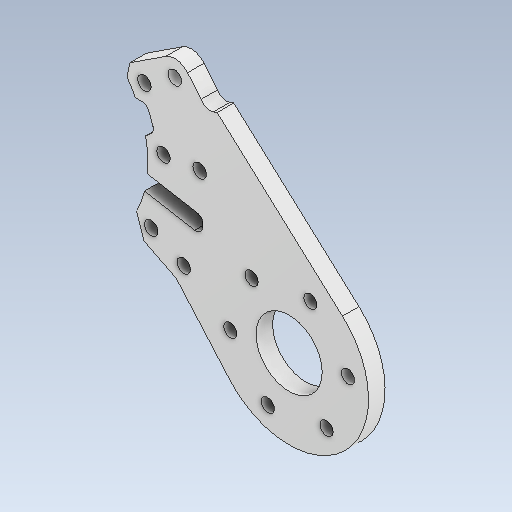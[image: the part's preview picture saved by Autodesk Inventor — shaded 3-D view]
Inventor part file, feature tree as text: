
AUTODESK INVENTOR PART (.ipt)
format: ipt  version: 2020 (Build 240168000, 168)  size: 461,312 bytes
history: native  units: mm
features: reference x17, extrude x7, sketch x7, thicken_offset x4, other x4, projected_geometry x3, chamfer x2, fillet x1, shell x1
ambient origin geometry x8: Origin, YZ Plane, XZ Plane, XY Plane, X Axis, Y Axis, Z Axis, Center Point
bodies: Solid1 (feature_tree)
feature tree (46):
  extrude  "Extrusion1"  Depth=10.0mm
  extrude  "Extrusion2"  Depth=10.0mm
  extrude  "Extrusion3"  Depth=5.0mm TaperAngle=0.0deg
  extrude  "Extrusion4"  Depth=5.0mm
  chamfer  "Chamfer1"  Distance=5.0mm
  chamfer  "Chamfer2"  Distance=5.0mm
  extrude  "Extrusion5"  Depth=5.0mm TaperAngle=45.0deg
  extrude  "Extrusion6"  Depth=5.0mm
  extrude  "Extrusion7"  Depth=5.0mm
  thicken_offset  "Thicken1"
  thicken_offset  "Thicken2"
  thicken_offset  "Thicken3"
  thicken_offset  "Thicken4"
  fillet  "Fillet1"  Radius=5.0mm
  sketch  "Sketch1"  dims[d0=48.0mm d1=10.0mm]
  reference  "Reference1"
  reference  "Reference2"
  reference  "Reference3"
  reference  "Reference4"
  reference  "Reference5"
  reference  "Reference6"
  reference  "Reference7"
  reference  "Reference8"
  reference  "Reference9"
  sketch  "Sketch2"  dims[d2=10.0mm d3=10.0mm]
  projected_geometry  "Projected Loop1"
  sketch  "Sketch3"  dims[d4=64.0mm d5=5.0mm d6=0.0mm]
  reference  "Reference10"
  sketch  "Sketch4"  dims[d7=5.0mm d8=0.0mm d9=5.0mm]
  projected_geometry  "Projected Loop2"
  sketch  "Sketch5"  dims[d10=16.0mm d11=5.0mm d12=0.0mm]
  reference  "Reference11"
  sketch  "Sketch6"  dims[d13=20.0mm d14=5.0mm d15=0.0mm]
  projected_geometry  "Projected Loop3"
  sketch  "Sketch7"  dims[d16=3.0mm d17=2.0mm d18=45.0deg d19=5.0mm d20=2.0mm d21=45.0deg d22=5.0mm d23=5.0mm d24=5.0mm d25=0.0mm d26=3.490659mm d27=3.490659mm d28=5.0mm d29=0.0mm d30=5.0mm d31=0.0mm d32=1.0mm d33=1.0mm d34=1.0mm d35=1.0mm d36=1.0mm d37=1.0mm d38=2.0mm d39=2.0mm d40=2.0mm]
  reference  "Reference12"
  reference  "Reference13"
  reference  "Reference14"
  reference  "Reference15"
  reference  "Reference16"
  reference  "Reference17"
  parser-record x1  (decoder bookkeeping rows leaked as tree rows — omitted from the tree; the rows remain in map.json)
  other  "reducer_3.iam"
  other  "motor_h_3_m:1"
  shell  "shell_4:1"  Thickness=3.490659mm
  other  "motor_h_1:1"
note: 1 file-system path scrubbed to <path> (originals preserved in map.json)
